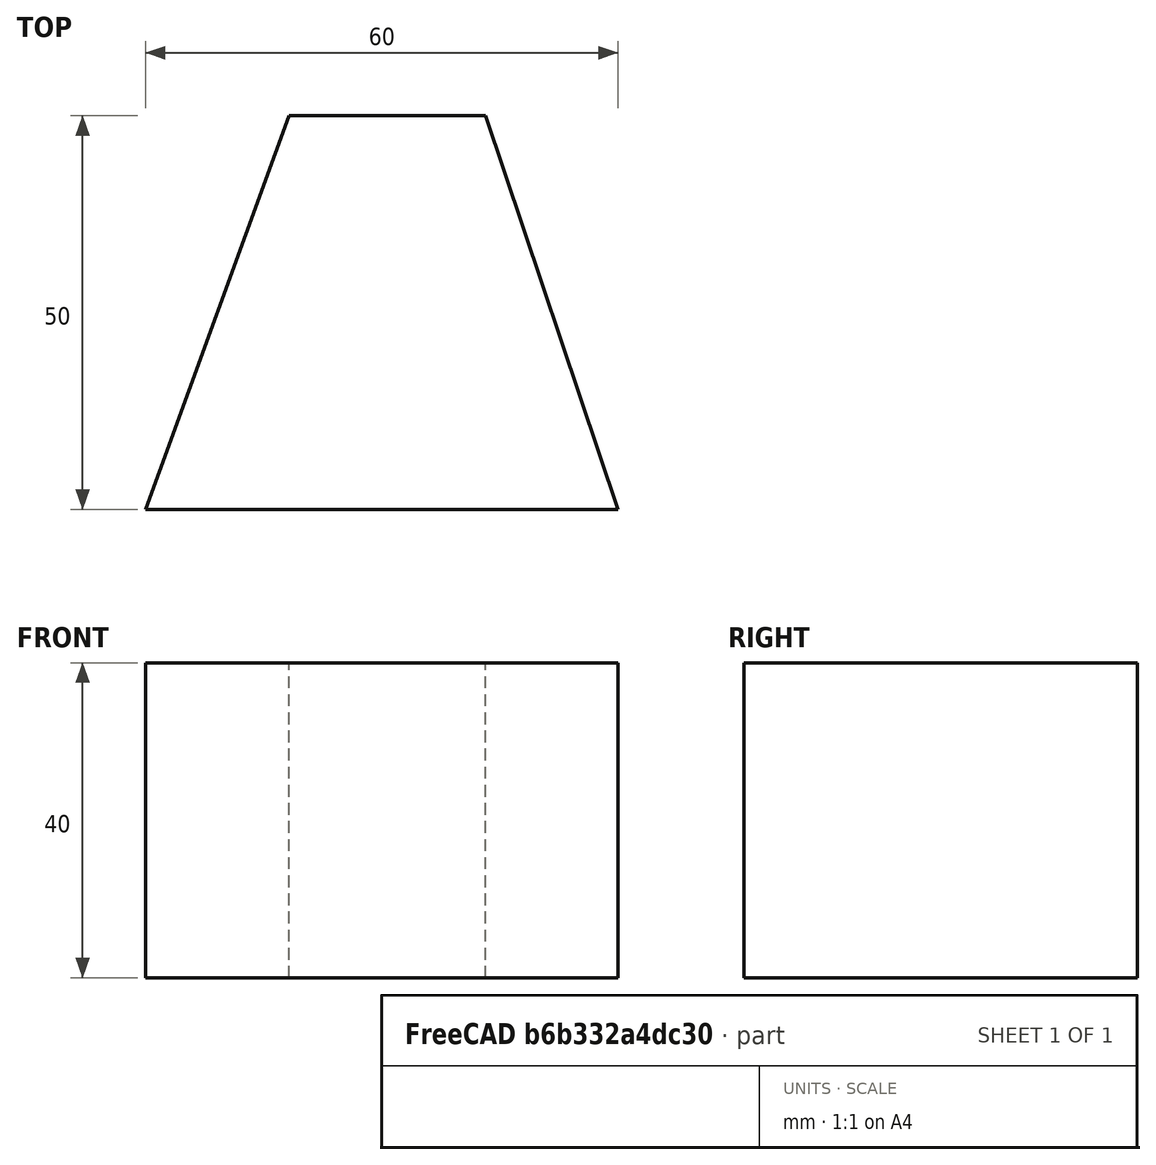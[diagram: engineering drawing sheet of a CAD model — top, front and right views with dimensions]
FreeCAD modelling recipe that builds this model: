
FCSTD DOCUMENT  (FreeCAD 0.19R)
Label: Trapezoid
License: All rights reserved
LicenseURL: http://en.wikipedia.org/wiki/All_rights_reserved
objects: Sketcher::SketchObject×1, PartDesign::Pad×1, PartDesign::Body×1
note: 4 computed .brp shape members not serialized (recipe doc carries the construction recipe); baked Part::Feature solids carry a one-line shape summary decoded from their .brp

FEATURE [Sketcher::SketchObject] Sketch
  FullyConstrained = true
  MapMode = 5
  Support = -> [XY_Plane]
  sketch-geometry (4):
    g0: LineSegment StartX=26.1985 StartY=58 StartZ=0 EndX=51.1985 EndY=58 EndZ=0
    g1: LineSegment StartX=51.1985 StartY=58 StartZ=0 EndX=68 EndY=8 EndZ=0
    g2: LineSegment StartX=68 StartY=8 StartZ=0 EndX=8 EndY=8 EndZ=0
    g3: LineSegment StartX=8 StartY=8 StartZ=0 EndX=26.1985 EndY=58 EndZ=0
  constraints (12):
    c: Coincident(g0,g1)
    c: Coincident(g1,g2)
    c: Coincident(g2,g3)
    c: Coincident(g3,g0)
    c: Horizontal(g0)
    c: Horizontal(g2)
    c: DistanceY(g-1,g2) = 8
    c: DistanceX(g-1,g2) = 8
    c: DistanceX(g2,g2) = 60
    c: DistanceY(g1,g0) = 50
    c: DistanceX(g0,g0) = 25
    c: Angle(g2,g3) = 1.22173
FEATURE [PartDesign::Pad] Pad
  Direction = (1,1,1)
  Length = 40
  Length2 = 100
  Profile = -> Sketch
  Type = 0
FEATURE [PartDesign::Body] Body
  Group = -> [Sketch,Pad]
  Origin = -> Origin
  Tip = -> Pad
